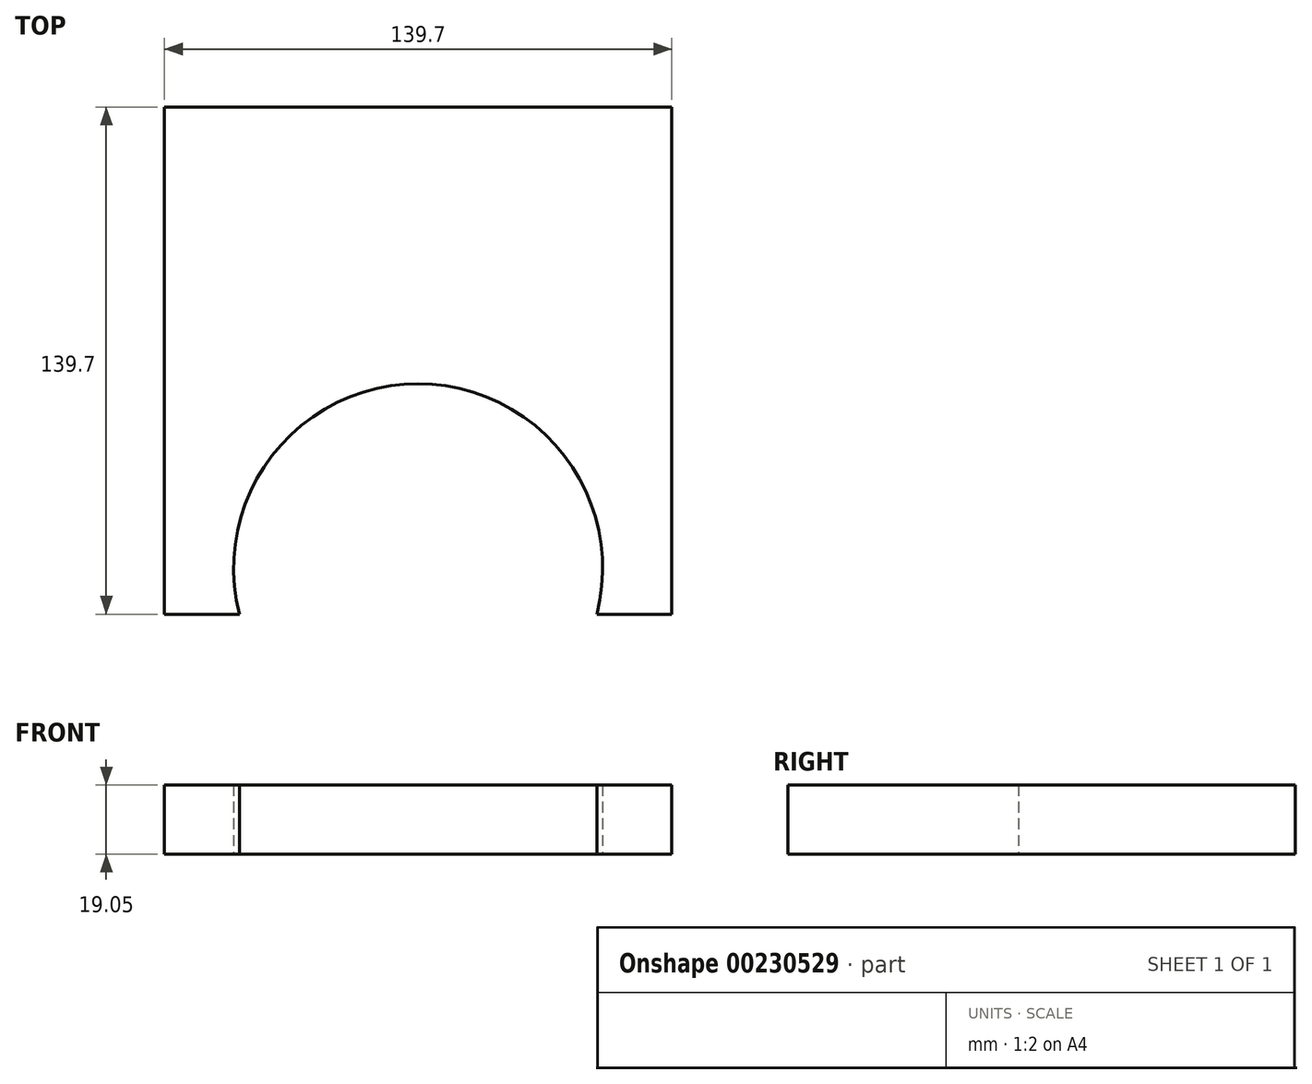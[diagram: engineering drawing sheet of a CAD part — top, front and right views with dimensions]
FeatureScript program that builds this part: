
annotation { "Feature Type Name" : "Feature", "Feature Type Description" : "" }
export const myFeature = defineFeature(function(context is Context, id is Id, definition is map)
    precondition{}
    {
        {
            var Q0;
            Q0=qCreatedBy(makeId("Top.planeOp"),FACE);
            var sketch = newSketch(context, id + "F0", { "sketchPlane" : qUnion([Q0])});
            skLineSegment(sketch, "E0.bottom", {"start": v(-69.85, -69.85) * mm, "end": v(-49.19, -69.85) * mm});
            skLineSegment(sketch, "E0.top", {"start": v(-69.85, 69.85) * mm, "end": v(69.85, 69.85) * mm});
            skLineSegment(sketch, "E0.left", {"start": v(-69.85, -69.85) * mm, "end": v(-69.85, 69.85) * mm});
            skLineSegment(sketch, "E0.right", {"start": v(69.85, -69.85) * mm, "end": v(69.85, 69.85) * mm});
            skPoint(sketch, "E0.middle", {"position": v(0, 0) * mm});
            skArc(sketch, "E1", {"start": v(49.19, -69.85) * mm, "mid": v(0, -6.35) * mm, "end": v(-49.19, -69.85) * mm});
            skLineSegment(sketch, "E2.trimOffspring", {"start": v(49.19, -69.85) * mm, "end": v(69.85, -69.85) * mm});
            skSolve(sketch);
        }
        {
            var Q0;
            Q0=makeQuery(id+"F0.imprint","IMPRINT",FACE,{"disambiguationData":[TD([[makeQuery(id+"F0.imprint","IMPRINT",EDGE,{"derivedFrom":sQuery(id+"F0.wireOp",EDGE,"E0.bottom")}),1.0]])]});
            extrude(context, id + "F1", {"entities" : qUnion([Q0]), "depth" : 19.05 * mm});
        }
    });
